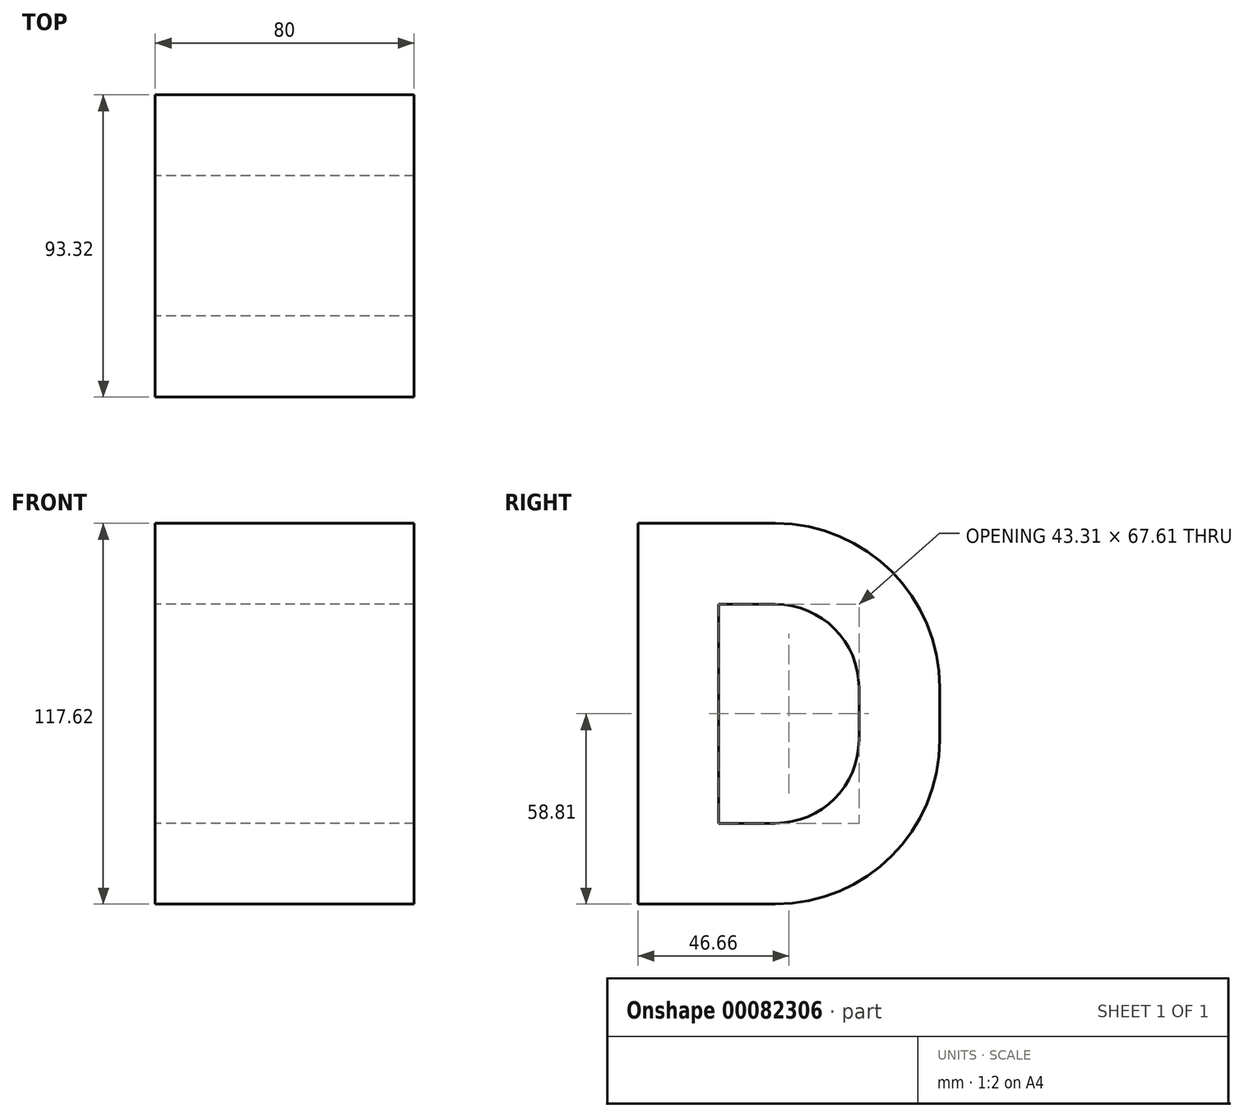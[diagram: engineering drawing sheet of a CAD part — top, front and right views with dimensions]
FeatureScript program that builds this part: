
annotation { "Feature Type Name" : "Feature", "Feature Type Description" : "" }
export const myFeature = defineFeature(function(context is Context, id is Id, definition is map)
    precondition{}
    {
        {
            var Q0;
            Q0=qCreatedBy(makeId("Right.planeOp"),FACE);
            var sketch = newSketch(context, id + "F0", { "sketchPlane" : qUnion([Q0])});
            skLineSegment(sketch, "E0.bottom", {"start": v(-4.14, 58.8) * mm, "end": v(-46.66, 58.8) * mm});
            skLineSegment(sketch, "E0.top", {"start": v(-4.14, -58.8) * mm, "end": v(-46.66, -58.8) * mm});
            skLineSegment(sketch, "E0.left", {"start": v(46.66, 8) * mm, "end": v(46.66, -8) * mm});
            skLineSegment(sketch, "E0.right", {"start": v(-46.66, 58.8) * mm, "end": v(-46.66, -58.8) * mm});
            skPoint(sketch, "E0.middle", {"position": v(0, 0) * mm});
            skPoint(sketch, "E1.visualSharp", {"position": v(46.66, 58.8) * mm});
            skArc(sketch, "E1.filletArc", {"start": v(46.66, 8) * mm, "mid": v(31.78, 43.93) * mm, "end": v(-4.14, 58.8) * mm});
            skPoint(sketch, "E2.visualSharp", {"position": v(46.66, -58.8) * mm});
            skArc(sketch, "E2.filletArc", {"start": v(-4.14, -58.8) * mm, "mid": v(31.78, -43.93) * mm, "end": v(46.66, -8) * mm});
            skArc(sketch, "E3.0", {"start": v(21.66, 8) * mm, "mid": v(14.1, 26.25) * mm, "end": v(-4.14, 33.8) * mm});
            skLineSegment(sketch, "E3.1", {"start": v(-21.66, 33.8) * mm, "end": v(-21.66, -33.8) * mm});
            skLineSegment(sketch, "E3.2", {"start": v(-4.14, -33.8) * mm, "end": v(-21.66, -33.8) * mm});
            skLineSegment(sketch, "E3.3", {"start": v(-4.14, 33.8) * mm, "end": v(-21.66, 33.8) * mm});
            skArc(sketch, "E3.4", {"start": v(-4.14, -33.8) * mm, "mid": v(14.1, -26.25) * mm, "end": v(21.66, -8) * mm});
            skLineSegment(sketch, "E3.5", {"start": v(21.66, 8) * mm, "end": v(21.66, -8) * mm});
            skSolve(sketch);
        }
        {
            var Q0;
            Q0=makeQuery(id+"F0.imprint","IMPRINT",FACE,{"disambiguationData":[TD([[makeQuery(id+"F0.imprint","IMPRINT",EDGE,{"derivedFrom":sQuery(id+"F0.wireOp",EDGE,"E0.bottom")}),1.0]])]});
            extrude(context, id + "F1", {"entities" : qUnion([Q0]), "endBound" : BoundingType.SYMMETRIC, "depth" : 80 * mm});
        }
    });
